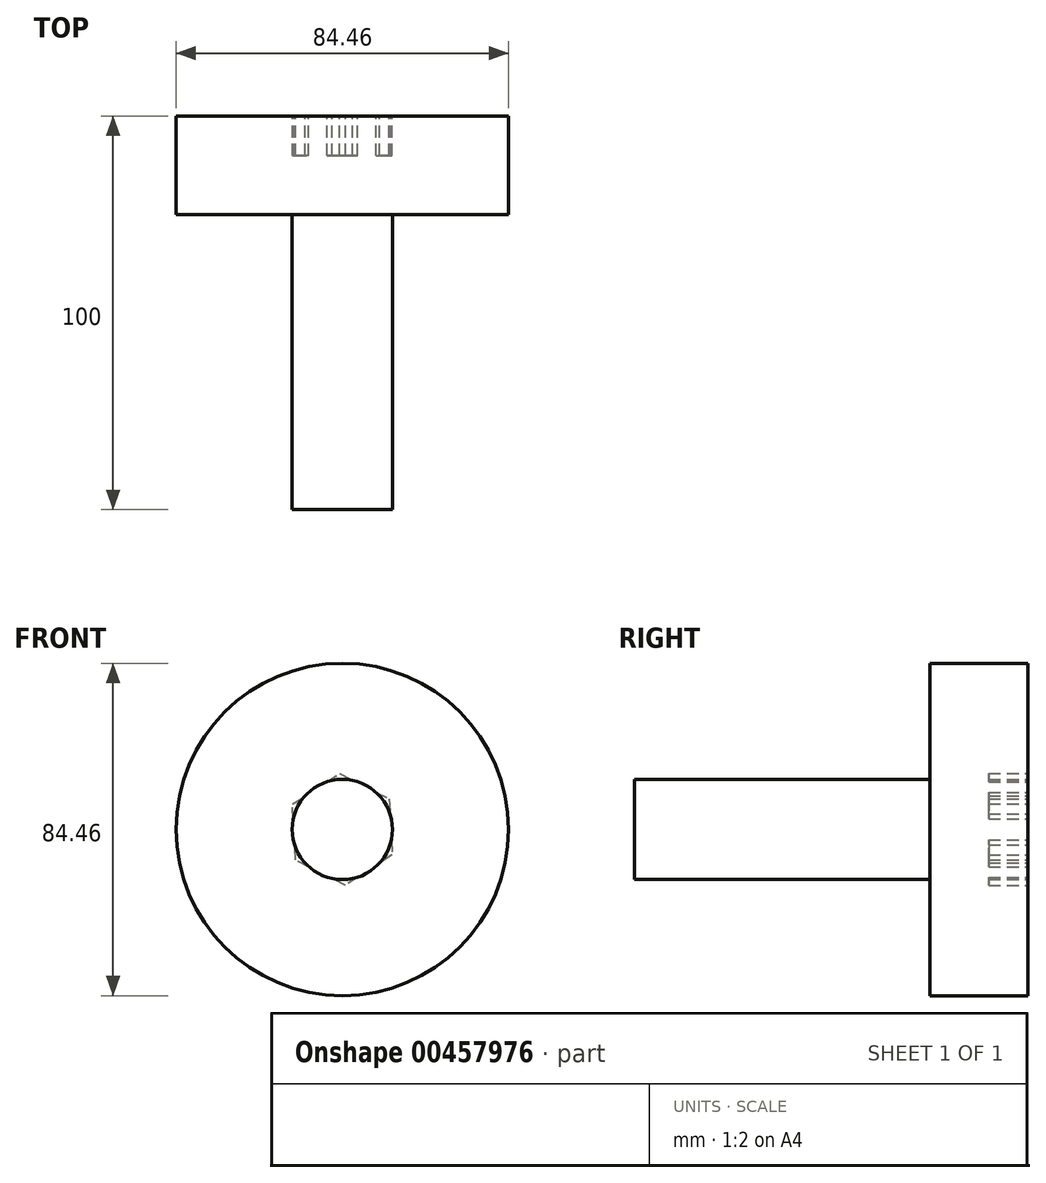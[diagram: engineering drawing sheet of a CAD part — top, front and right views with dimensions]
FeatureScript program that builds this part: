
annotation { "Feature Type Name" : "Feature", "Feature Type Description" : "" }
export const myFeature = defineFeature(function(context is Context, id is Id, definition is map)
    precondition{}
    {
        {
            var Q0;
            Q0=qCreatedBy(makeId("Front.planeOp"),FACE);
            var sketch = newSketch(context, id + "F0", { "sketchPlane" : qUnion([Q0])});
            skCircle(sketch, "E0", {"center": v(0, 0) * mm, "radius": 42.23 * mm});
            skSolve(sketch);
        }
        {
            var Q0;
            Q0 = qSketchRegion(id + "F0", true);
            extrude(context, id + "F1", {"entities" : qUnion([Q0]), "depth" : 25 * mm});
        }
        {
            var Q0;
            Q0=qCreatedBy(makeId("Front.planeOp"),FACE);
            var sketch = newSketch(context, id + "F2", { "sketchPlane" : qUnion([Q0])});
            skCircle(sketch, "E1.cCircle", {"center": v(0, 0) * mm, "radius": 12.3 * mm, "construction": true});
            skLineSegment(sketch, "E1.0", {"start": v(12.66, -6.43) * mm, "end": v(0.76, -14.18) * mm});
            skLineSegment(sketch, "E1.1", {"start": v(0.76, -14.18) * mm, "end": v(-11.9, -7.75) * mm});
            skLineSegment(sketch, "E1.2", {"start": v(-11.9, -7.75) * mm, "end": v(-12.66, 6.43) * mm});
            skLineSegment(sketch, "E1.3", {"start": v(-12.66, 6.43) * mm, "end": v(-0.76, 14.18) * mm});
            skLineSegment(sketch, "E1.4", {"start": v(-0.76, 14.18) * mm, "end": v(11.9, 7.75) * mm});
            skLineSegment(sketch, "E1.5", {"start": v(11.9, 7.75) * mm, "end": v(12.66, -6.43) * mm});
            skPoint(sketch, "E1.0.midPoint", {"position": v(6.71, -10.3) * mm});
            skSolve(sketch);
        }
        {
            var Q0;
            Q0 = qSketchRegion(id + "F2", true);
            extrude(context, id + "F3", {"entities" : qUnion([Q0]), "operationType" : NewBodyOperationType.REMOVE, "depth" : 10 * mm});
        }
        {
            var Q0;
            Q0=qCreatedBy(makeId("Front.planeOp"),FACE);
            var sketch = newSketch(context, id + "F4", { "sketchPlane" : qUnion([Q0])});
            skCircle(sketch, "E2", {"center": v(0, 0) * mm, "radius": 12.74 * mm});
            skSolve(sketch);
        }
        {
            var Q0;
            Q0 = qSketchRegion(id + "F4", true);
            extrude(context, id + "F5", {"entities" : qUnion([Q0]), "operationType" : NewBodyOperationType.ADD, "depth" : 100 * mm});
        }
    });
